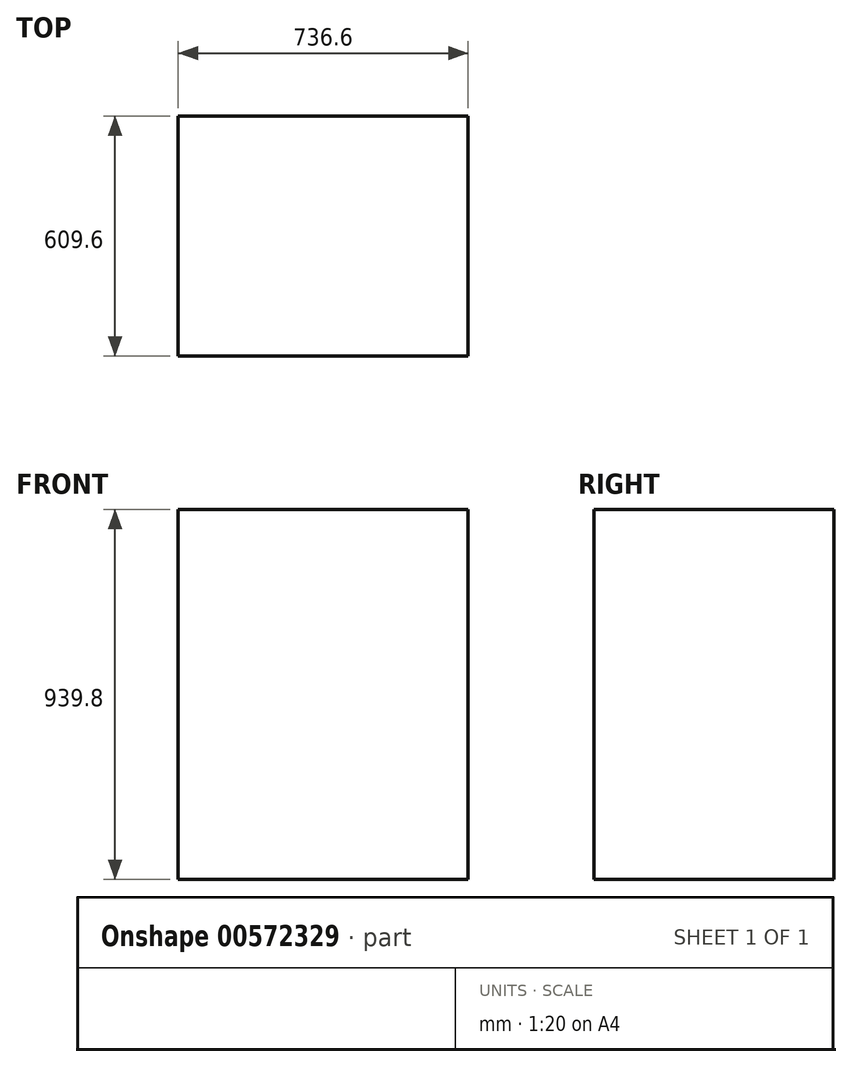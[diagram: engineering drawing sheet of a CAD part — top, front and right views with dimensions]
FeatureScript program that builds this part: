
annotation { "Feature Type Name" : "Feature", "Feature Type Description" : "" }
export const myFeature = defineFeature(function(context is Context, id is Id, definition is map)
    precondition{}
    {
        {
            var Q0;
            Q0=qCreatedBy(makeId("Right.planeOp"),FACE);
            var sketch = newSketch(context, id + "F0", { "sketchPlane" : qUnion([Q0])});
            skLineSegment(sketch, "E0.bottom", {"start": v(-436.56, -755.65) * mm, "end": v(173.04, -755.65) * mm});
            skLineSegment(sketch, "E0.top", {"start": v(-436.56, 184.15) * mm, "end": v(173.04, 184.15) * mm});
            skLineSegment(sketch, "E0.left", {"start": v(-436.56, -755.65) * mm, "end": v(-436.56, 184.15) * mm});
            skLineSegment(sketch, "E0.right", {"start": v(173.04, -755.65) * mm, "end": v(173.04, 184.15) * mm});
            skLineSegment(sketch, "E1.bottom", {"start": v(173.04, 184.15) * mm, "end": v(71.44, 184.15) * mm});
            skLineSegment(sketch, "E1.top", {"start": v(173.04, 387.35) * mm, "end": v(109.54, 387.35) * mm});
            skLineSegment(sketch, "E1.left", {"start": v(173.04, 184.15) * mm, "end": v(173.04, 387.35) * mm});
            skLineSegment(sketch, "E2", {"start": v(71.44, 184.15) * mm, "end": v(109.54, 387.35) * mm});
            skSolve(sketch);
        }
        {
            var Q0;
            Q0=makeQuery(id+"F0.imprint","IMPRINT",FACE,{"disambiguationData":[TD([[makeQuery(id+"F0.imprint","IMPRINT",EDGE,{"derivedFrom":sQuery(id+"F0.wireOp",EDGE,"E0.bottom")}),1.0]])]});
            var Q1;
            Q1=makeQuery(id+"F0.imprint","IMPRINT",FACE,{"disambiguationData":[TD([[makeQuery(id+"F0.imprint","IMPRINT",EDGE,{"derivedFrom":sQuery(id+"F0.wireOp",EDGE,"E1.bottom")}),-1.0]])]});
            extrude(context, id + "F1", {"entities" : qUnion([Q0, Q1]), "depth" : 736.6 * mm, "offsetDistance" : 25.4 * mm});
        }
    });
